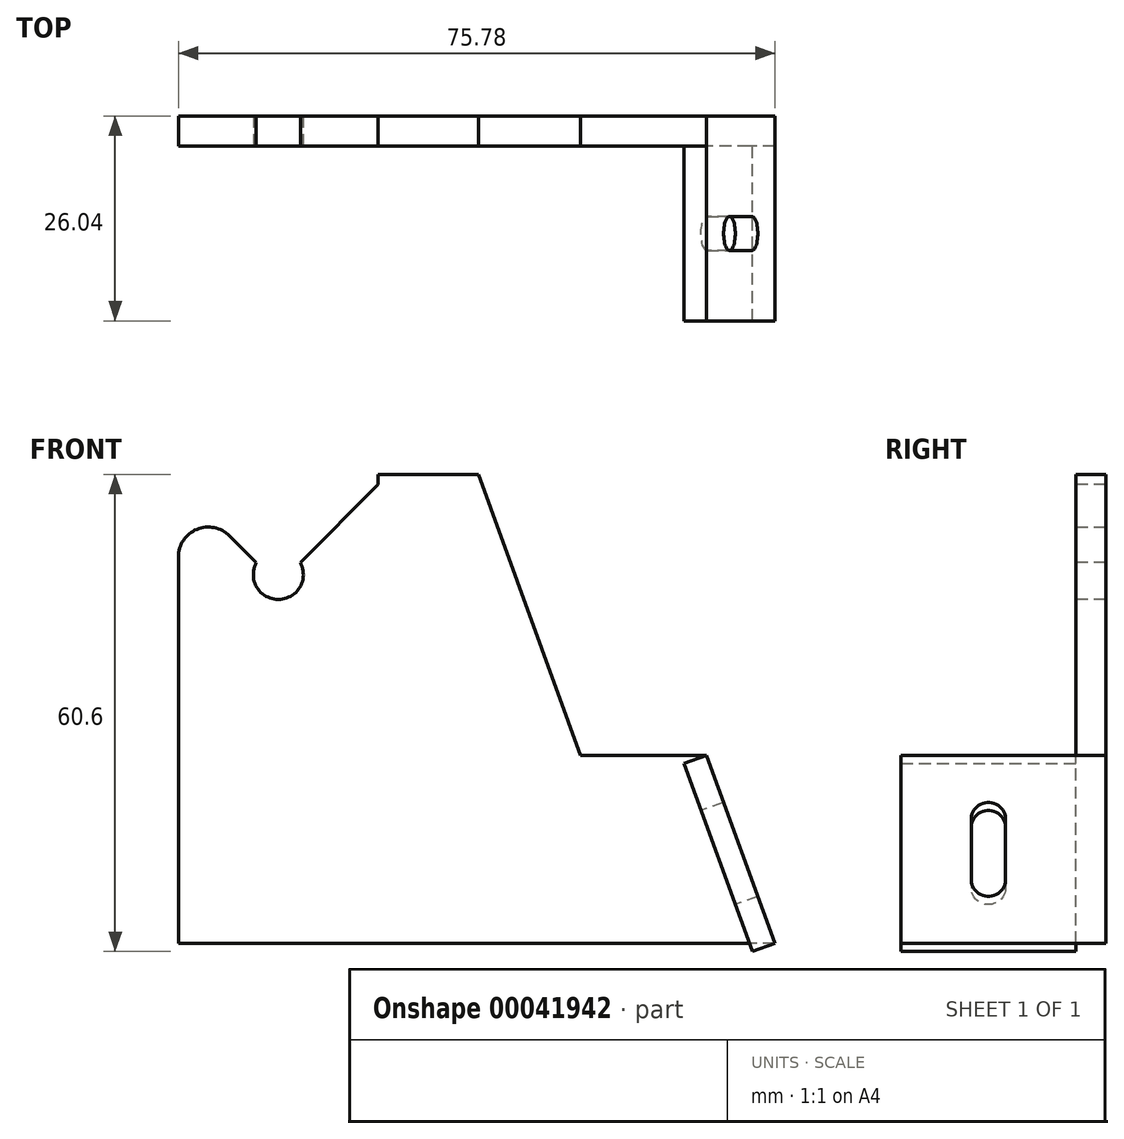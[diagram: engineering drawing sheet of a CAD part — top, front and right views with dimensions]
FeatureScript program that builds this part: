
annotation { "Feature Type Name" : "Feature", "Feature Type Description" : "" }
export const myFeature = defineFeature(function(context is Context, id is Id, definition is map)
    precondition{}
    {
        {
            var Q0;
            Q0=qCreatedBy(makeId("Front.planeOp"),FACE);
            var sketch = newSketch(context, id + "F0", { "sketchPlane" : qUnion([Q0])});
            skLineSegment(sketch, "E0", {"start": v(2.86, -61.1) * mm, "end": v(11.55, -84.96) * mm});
            skLineSegment(sketch, "E1", {"start": v(11.55, -84.96) * mm, "end": v(8.69, -86) * mm});
            skLineSegment(sketch, "E2", {"start": v(8.69, -86) * mm, "end": v(0, -62.13) * mm});
            skLineSegment(sketch, "E3", {"start": v(0, -62.13) * mm, "end": v(2.86, -61.1) * mm});
            skLineSegment(sketch, "E4", {"start": v(0, 0) * mm, "end": v(43.58, 0) * mm, "construction": true});
            skPoint(sketch, "E5", {"position": v(7.2, -73.03) * mm});
            skSolve(sketch);
        }
        {
            var Q0;
            Q0=qSketchRegion(id+"F0",true);
            extrude(context, id + "F1", {"entities" : qUnion([Q0]), "depth" : 22.22 * mm});
        }
        {
            var Q0;
            Q0=makeQuery(id+"F1.opExtrude","SWEPT_FACE",FACE,{"disambiguationData":[OSD([sQuery(id+"F0.wireOp",EDGE,"E2")])]});
            var sketch = newSketch(context, id + "F2", { "sketchPlane" : qUnion([Q0])});
            skLineSegment(sketch, "E6.bottom", {"start": v(8.95, -64.74) * mm, "end": v(13.27, -64.74) * mm});
            skLineSegment(sketch, "E6.top", {"start": v(8.95, -77.44) * mm, "end": v(13.27, -77.44) * mm});
            skLineSegment(sketch, "E6.left", {"start": v(8.95, -64.74) * mm, "end": v(8.95, -77.44) * mm});
            skLineSegment(sketch, "E6.right", {"start": v(13.27, -64.74) * mm, "end": v(13.27, -77.44) * mm});
            skLineSegment(sketch, "E7.bottom", {"start": v(8.95, -86.96) * mm, "end": v(13.27, -86.96) * mm});
            skLineSegment(sketch, "E7.top", {"start": v(8.95, -99.66) * mm, "end": v(13.27, -99.66) * mm});
            skLineSegment(sketch, "E7.left", {"start": v(8.95, -86.96) * mm, "end": v(8.95, -99.66) * mm});
            skLineSegment(sketch, "E7.right", {"start": v(13.27, -86.96) * mm, "end": v(13.27, -99.66) * mm});
            skPoint(sketch, "E8", {"position": v(13.27, -71.09) * mm});
            skLineSegment(sketch, "E9", {"start": v(11.11, -58.39) * mm, "end": v(11.11, -64.74) * mm, "construction": true});
            skSolve(sketch);
        }
        {
            var Q0;
            Q0=qSketchRegion(id+"F2",true);
            extrude(context, id + "F3", {"entities" : qUnion([Q0]), "operationType" : NewBodyOperationType.REMOVE, "endBound" : BoundingType.THROUGH_ALL, "oppositeDirection" : true, "depth" : 25.4 * mm});
        }
        {
            var Q0;
            Q0=makeQuery(id+"F3.boolean.opBoolean","COPY",EDGE,{"derivedFrom":makeQuery(id+"F3.opExtrude","SWEPT_EDGE",EDGE,{"disambiguationData":[OSD([sQuery(id+"F2.wireOp",EDGE,"E6.bottom"),sQuery(id+"F2.wireOp",EDGE,"E6.left")])]})});
            var Q1;
            Q1=makeQuery(id+"F3.boolean.opBoolean","COPY",EDGE,{"derivedFrom":makeQuery(id+"F3.opExtrude","SWEPT_EDGE",EDGE,{"disambiguationData":[OSD([sQuery(id+"F2.wireOp",EDGE,"E7.bottom"),sQuery(id+"F2.wireOp",EDGE,"E7.left")])]})});
            var Q2;
            Q2=makeQuery(id+"F3.boolean.opBoolean","COPY",EDGE,{"derivedFrom":makeQuery(id+"F3.opExtrude","SWEPT_EDGE",EDGE,{"disambiguationData":[OSD([sQuery(id+"F2.wireOp",EDGE,"E7.bottom"),sQuery(id+"F2.wireOp",EDGE,"E7.right")])]})});
            var Q3;
            Q3=makeQuery(id+"F3.boolean.opBoolean","COPY",EDGE,{"derivedFrom":makeQuery(id+"F3.opExtrude","SWEPT_EDGE",EDGE,{"disambiguationData":[OSD([sQuery(id+"F2.wireOp",EDGE,"E6.bottom"),sQuery(id+"F2.wireOp",EDGE,"E6.right")])]})});
            var Q4;
            Q4=makeQuery(id+"F3.boolean.opBoolean","COPY",EDGE,{"derivedFrom":makeQuery(id+"F3.opExtrude","SWEPT_EDGE",EDGE,{"disambiguationData":[OSD([sQuery(id+"F2.wireOp",EDGE,"E6.top"),sQuery(id+"F2.wireOp",EDGE,"E6.right")])]})});
            var Q5;
            Q5=makeQuery(id+"F3.boolean.opBoolean","COPY",EDGE,{"derivedFrom":makeQuery(id+"F3.opExtrude","SWEPT_EDGE",EDGE,{"disambiguationData":[OSD([sQuery(id+"F2.wireOp",EDGE,"E7.top"),sQuery(id+"F2.wireOp",EDGE,"E7.right")])]})});
            var Q6;
            Q6=makeQuery(id+"F3.boolean.opBoolean","COPY",EDGE,{"derivedFrom":makeQuery(id+"F3.opExtrude","SWEPT_EDGE",EDGE,{"disambiguationData":[OSD([sQuery(id+"F2.wireOp",EDGE,"E7.top"),sQuery(id+"F2.wireOp",EDGE,"E7.left")])]})});
            var Q7;
            Q7=makeQuery(id+"F3.boolean.opBoolean","COPY",EDGE,{"derivedFrom":makeQuery(id+"F3.opExtrude","SWEPT_EDGE",EDGE,{"disambiguationData":[OSD([sQuery(id+"F2.wireOp",EDGE,"E6.top"),sQuery(id+"F2.wireOp",EDGE,"E6.left")])]})});
            fillet(context, id + "F4", {"entities" : qUnion([Q0, Q1, Q2, Q3, Q4, Q5, Q6, Q7]), "radius" : 2.16 * mm, "tangentPropagation" : true, "allowEdgeOverflow" : false});
        }
        {
            var Q0;
            Q0=qCreatedBy(makeId("Front.planeOp"),FACE);
            var sketch = newSketch(context, id + "F5", { "sketchPlane" : qUnion([Q0])});
            skLineSegment(sketch, "E10", {"start": v(2.86, -61.1) * mm, "end": v(11.55, -84.96) * mm});
            skLineSegment(sketch, "E11", {"start": v(11.55, -84.96) * mm, "end": v(-64.23, -84.96) * mm});
            skLineSegment(sketch, "E12", {"start": v(-64.23, -84.96) * mm, "end": v(-64.23, -25.4) * mm});
            skLineSegment(sketch, "E13", {"start": v(-64.23, -25.4) * mm, "end": v(-26.13, -25.4) * mm});
            skLineSegment(sketch, "E14", {"start": v(-26.13, -25.4) * mm, "end": v(-13.14, -61.1) * mm});
            skLineSegment(sketch, "E15", {"start": v(-13.14, -61.1) * mm, "end": v(2.86, -61.1) * mm});
            skCircle(sketch, "E16", {"center": v(-51.53, -38.1) * mm, "radius": 3.18 * mm});
            skSolve(sketch);
        }
        {
            var Q0;
            Q0=qSketchRegion(id+"F5",true);
            extrude(context, id + "F6", {"entities" : qUnion([Q0]), "operationType" : NewBodyOperationType.ADD, "oppositeDirection" : true, "depth" : 3.8 * mm});
        }
        {
            var Q0;
            Q0=qCreatedBy(makeId("Front.planeOp"),FACE);
            var sketch = newSketch(context, id + "F7", { "sketchPlane" : qUnion([Q0])});
            skLineSegment(sketch, "E17", {"start": v(-51.53, -39.39) * mm, "end": v(-65.52, -25.4) * mm});
            skLineSegment(sketch, "E18", {"start": v(-65.52, -25.4) * mm, "end": v(-38.83, -25.4) * mm});
            skLineSegment(sketch, "E19", {"start": v(-38.83, -25.4) * mm, "end": v(-38.83, -26.69) * mm});
            skLineSegment(sketch, "E20", {"start": v(-38.83, -26.69) * mm, "end": v(-51.53, -39.39) * mm});
            skLineSegment(sketch, "E21", {"start": v(-54.32, -36.6) * mm, "end": v(-48.74, -36.6) * mm, "construction": true});
            skSolve(sketch);
        }
        {
            var Q0;
            Q0 = qSketchRegion(id + "F7", true);
            extrude(context, id + "F8", {"entities" : qUnion([Q0]), "operationType" : NewBodyOperationType.REMOVE, "oppositeDirection" : true, "depth" : 25.4 * mm});
        }
        {
            var Q0;
            Q0=makeQuery(id+"F8.boolean.opBoolean","INTERSECT",EDGE,{"derivedFrom":[makeQuery(id+"F6.opExtrude","SWEPT_FACE",FACE,{"disambiguationData":[OSD([sQuery(id+"F5.wireOp",EDGE,"E12")])]}),makeQuery(id+"F8.opExtrude","SWEPT_FACE",FACE,{"disambiguationData":[OSD([sQuery(id+"F7.wireOp",EDGE,"E17")])]})]});
            fillet(context, id + "F9", {"entities" : qUnion([Q0]), "radius" : 3.8 * mm, "tangentPropagation" : true, "allowEdgeOverflow" : false});
        }
    });
